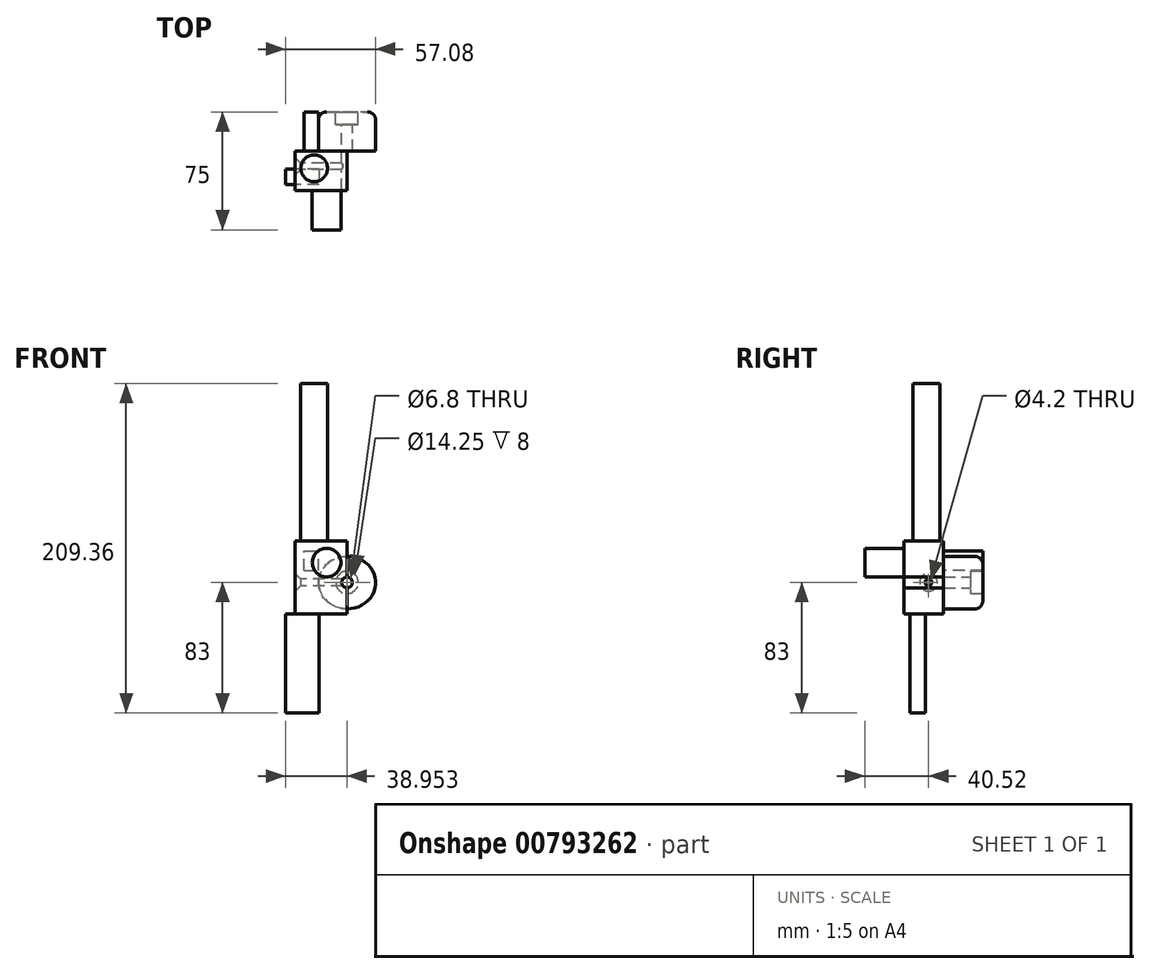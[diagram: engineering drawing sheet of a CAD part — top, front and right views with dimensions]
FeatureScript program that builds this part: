
annotation { "Feature Type Name" : "Feature", "Feature Type Description" : "" }
export const myFeature = defineFeature(function(context is Context, id is Id, definition is map)
    precondition{}
    {
        {
            var Q0;
            Q0=qCreatedBy(makeId("Front.planeOp"),FACE);
            var sketch = newSketch(context, id + "F0", { "sketchPlane" : qUnion([Q0])});
            skLineSegment(sketch, "E0.top", {"start": v(12.98, -20) * mm, "end": v(-20, -20) * mm});
            skLineSegment(sketch, "E0.left", {"start": v(12.98, 26.36) * mm, "end": v(12.98, -20) * mm});
            skLineSegment(sketch, "E0.right", {"start": v(-20, 26.36) * mm, "end": v(-20, -20) * mm});
            skLineSegment(sketch, "E1", {"start": v(12.98, 26.36) * mm, "end": v(-20, 26.36) * mm});
            skSolve(sketch);
        }
        {
            var Q0;
            Q0 = qSketchRegion(id + "F0", true);
            extrude(context, id + "F1", {"entities" : qUnion([Q0]), "depth" : 25 * mm, "offsetDistance" : 25 * mm});
        }
        {
            var Q0;
            Q0=makeQuery(id+"F1.opExtrude","CAP_FACE",FACE,{"disambiguationData":[OSD([sQuery(id+"F0.wireOp",EDGE,"E0.top"),sQuery(id+"F0.wireOp",EDGE,"E0.left"),sQuery(id+"F0.wireOp",EDGE,"E0.right"),sQuery(id+"F0.wireOp",EDGE,"E1")])],"isStart":false});
            var sketch = newSketch(context, id + "F2", { "sketchPlane" : qUnion([Q0])});
            skCircle(sketch, "E2", {"center": v(0, 12.57) * mm, "radius": 9.08 * mm});
            skSolve(sketch);
        }
        {
            var Q0;
            Q0=makeQuery(id+"F2.imprint","IMPRINT",FACE,{"disambiguationData":[TD([[makeQuery(id+"F2.imprint","IMPRINT",EDGE,{"derivedFrom":sQuery(id+"F2.wireOp",EDGE,"E2")}),1.0]])]});
            extrude(context, id + "F3", {"entities" : qUnion([Q0]), "operationType" : NewBodyOperationType.ADD, "depth" : 25 * mm, "offsetDistance" : 25 * mm});
        }
        {
            var Q0;
            Q0=makeQuery(id+"F1.opExtrude","CAP_FACE",FACE,{"disambiguationData":[OSD([sQuery(id+"F0.wireOp",EDGE,"E0.top"),sQuery(id+"F0.wireOp",EDGE,"E0.left"),sQuery(id+"F0.wireOp",EDGE,"E0.right"),sQuery(id+"F0.wireOp",EDGE,"E1")])],"isStart":true});
            var sketch = newSketch(context, id + "F4", { "sketchPlane" : qUnion([Q0])});
            skEllipse(sketch, "E3", {"center": v(-12.98, -0.13) * mm, "majorRadius": 18.12 * mm, "minorRadius": 16.69 * mm, "majorAxis": v(1, 0)});
            skSolve(sketch);
        }
        {
            var Q0;
            {var subQ0=sQuery(id+"F4.wireOp",EDGE,"E3");var subQ1=makeQuery(id+"F1.opExtrude","CAP_EDGE",EDGE,{"disambiguationData":[OSD([sQuery(id+"F0.wireOp",EDGE,"E0.left")])],"isStart":true});var subQ2=makeQuery(id+"F4.imprint","INTERSECT",VERTEX,{"disambiguationData":[OD(0.0)],"derivedFrom":[subQ1,subQ0]});Q0=makeQuery(id+"F4.imprint","IMPRINT",FACE,{"disambiguationData":[TD([[makeQuery(id+"F4.imprint","IMPRINT",EDGE,{"disambiguationData":[TD([[subQ2,1.0]])],"derivedFrom":subQ0}),1.0]])]});}
            var Q1;
            {var subQ0=sQuery(id+"F4.wireOp",EDGE,"E3");var subQ1=makeQuery(id+"F1.opExtrude","CAP_EDGE",EDGE,{"disambiguationData":[OSD([sQuery(id+"F0.wireOp",EDGE,"E0.left")])],"isStart":true});var subQ2=makeQuery(id+"F4.imprint","INTERSECT",VERTEX,{"disambiguationData":[OD(0.0)],"derivedFrom":[subQ1,subQ0]});Q1=makeQuery(id+"F4.imprint","IMPRINT",FACE,{"disambiguationData":[TD([[makeQuery(id+"F4.imprint","IMPRINT",EDGE,{"disambiguationData":[TD([[subQ2,-1.0]])],"derivedFrom":subQ0}),1.0]])]});}
            extrude(context, id + "F5", {"entities" : qUnion([Q0, Q1]), "operationType" : NewBodyOperationType.ADD, "depth" : 25 * mm, "offsetDistance" : 25 * mm});
        }
        {
            var Q0;
            Q0=makeQuery(id+"F5.opExtrude","CAP_FACE",FACE,{"disambiguationData":[OSD([sQuery(id+"F4.wireOp",EDGE,"E3")])],"isStart":false});
            var sketch = newSketch(context, id + "F6", { "sketchPlane" : qUnion([Q0])});
            skCircle(sketch, "E4", {"center": v(-12.98, 0) * mm, "radius": 7.85 * mm});
            skPoint(sketch, "E4.centerSnap0", {"position": v(-12.98, -16.82) * mm});
            skSolve(sketch);
        }
        {
            var Q0;
            Q0=sQuery(id+"F6.wireOp",VERTEX,"E4.center");
            var Q1;
            Q1=makeQuery(id+"F1.opExtrude","SWEPT_BODY",BODY,{"disambiguationData":[OSD([sQuery(id+"F0.wireOp",EDGE,"E0.top"),sQuery(id+"F0.wireOp",EDGE,"E0.left"),sQuery(id+"F0.wireOp",EDGE,"E0.right"),sQuery(id+"F0.wireOp",EDGE,"E1")])]});
            hole(context, id + "F7", {"style" : HoleStyle.C_BORE, "endStyle" : HoleEndStyle.THROUGH, "standardTappedOrClearance" : lookupTablePath({ "standard" : "ISO", "fit" : "Normal", "engagement" : "75%", "pitch" : "1.25 mm", "size" : "M8", "type" : "Tapped" }), "standardBlindInLast" : lookupTablePath({ "fit" : "Standard", "standard" : "ISO", "engagement" : "75%", "pitch" : "1.25 mm", "size" : "M8", "type" : "Tapped" }), "holeDiameter" : 6.8 * mm, "cBoreDiameter" : 14.25 * mm, "cBoreDepth" : 8 * mm, "majorDiameter" : 8 * mm, "showTappedDepth" : true, "isTappedThrough" : true, "tappedDepth" : 12 * mm, "tapClearance" : 3, "locations" : qUnion([Q0]), "scope" : qUnion([Q1])});
        }
        {
            var Q0;
            Q0=makeQuery(id+"F1.opExtrude","SWEPT_FACE",FACE,{"disambiguationData":[OSD([sQuery(id+"F0.wireOp",EDGE,"E0.right")])]});
            var sketch = newSketch(context, id + "F8", { "sketchPlane" : qUnion([Q0])});
            skPoint(sketch, "E5", {"position": v(9.48, 0) * mm});
            skSolve(sketch);
        }
        {
            var Q0;
            Q0=sQuery(id+"F8.wireOp",VERTEX,"E5");
            var Q1;
            Q1=makeQuery(id+"F1.opExtrude","SWEPT_BODY",BODY,{"disambiguationData":[OSD([sQuery(id+"F0.wireOp",EDGE,"E0.top"),sQuery(id+"F0.wireOp",EDGE,"E0.left"),sQuery(id+"F0.wireOp",EDGE,"E0.right"),sQuery(id+"F0.wireOp",EDGE,"E1")])]});
            hole(context, id + "F9", {"style" : HoleStyle.C_SINK, "endStyle" : HoleEndStyle.THROUGH, "standardTappedOrClearance" : lookupTablePath({ "standard" : "ISO", "fit" : "Normal", "engagement" : "75%", "pitch" : "0.8 mm", "size" : "M5", "type" : "Tapped" }), "standardBlindInLast" : lookupTablePath({ "fit" : "Standard", "standard" : "ISO", "engagement" : "75%", "pitch" : "0.8 mm", "size" : "M5", "type" : "Tapped" }), "holeDiameter" : 4.2 * mm, "cSinkDiameter" : 11.2 * mm, "cSinkAngle" : 90 * degree, "majorDiameter" : 5 * mm, "showTappedDepth" : true, "isTappedThrough" : true, "tappedDepth" : 12 * mm, "tapClearance" : 3, "locations" : qUnion([Q0]), "scope" : qUnion([Q1])});
        }
        {
            var Q0;
            Q0=makeQuery(id+"F1.opExtrude","SWEPT_FACE",FACE,{"disambiguationData":[OSD([sQuery(id+"F0.wireOp",EDGE,"E1")])]});
            var sketch = newSketch(context, id + "F10", { "sketchPlane" : qUnion([Q0])});
            skCircle(sketch, "E6", {"center": v(-7.9, -10.8) * mm, "radius": 8.51 * mm});
            skSolve(sketch);
        }
        {
            var Q0;
            Q0=makeQuery(id+"F10.imprint","IMPRINT",FACE,{"disambiguationData":[TD([[makeQuery(id+"F10.imprint","IMPRINT",EDGE,{"derivedFrom":sQuery(id+"F10.wireOp",EDGE,"E6")}),1.0]])]});
            extrude(context, id + "F11", {"entities" : qUnion([Q0]), "operationType" : NewBodyOperationType.ADD, "depth" : 100 * mm, "offsetDistance" : 25 * mm});
        }
        {
            var Q0;
            Q0=makeQuery(id+"F1.opExtrude","CAP_FACE",FACE,{"disambiguationData":[OSD([sQuery(id+"F0.wireOp",EDGE,"E0.top"),sQuery(id+"F0.wireOp",EDGE,"E0.left"),sQuery(id+"F0.wireOp",EDGE,"E0.right"),sQuery(id+"F0.wireOp",EDGE,"E1")])],"isStart":true});
            var sketch = newSketch(context, id + "F12", { "sketchPlane" : qUnion([Q0])});
            skPoint(sketch, "E7.oppositeSnap0", {"position": v(5.14, -0.13) * mm});
            skLineSegment(sketch, "E7.bottom", {"start": v(14.3, 7.5) * mm, "end": v(5.14, 7.5) * mm});
            skLineSegment(sketch, "E7.top", {"start": v(14.3, 20) * mm, "end": v(5.14, 20) * mm});
            skLineSegment(sketch, "E7.left", {"start": v(14.3, 7.5) * mm, "end": v(14.3, 20) * mm});
            skLineSegment(sketch, "E7.right", {"start": v(5.14, 7.5) * mm, "end": v(5.14, 20) * mm});
            skSolve(sketch);
        }
        {
            var Q0;
            Q0=makeQuery(id+"F12.imprint","IMPRINT",FACE,{"disambiguationData":[TD([[makeQuery(id+"F12.imprint","IMPRINT",EDGE,{"derivedFrom":sQuery(id+"F12.wireOp",EDGE,"E7.bottom")}),-1.0]])]});
            extrude(context, id + "F13", {"entities" : qUnion([Q0]), "operationType" : NewBodyOperationType.ADD, "depth" : 25 * mm, "offsetDistance" : 25 * mm});
        }
        {
            var Q0;
            Q0=makeQuery(id+"F1.opExtrude","SWEPT_FACE",FACE,{"disambiguationData":[OSD([sQuery(id+"F0.wireOp",EDGE,"E0.top")])]});
            var sketch = newSketch(context, id + "F14", { "sketchPlane" : qUnion([Q0])});
            skLineSegment(sketch, "E8.bottom", {"start": v(-4.65, 11.38) * mm, "end": v(-25.97, 11.38) * mm});
            skLineSegment(sketch, "E8.top", {"start": v(-4.65, 21.17) * mm, "end": v(-25.97, 21.17) * mm});
            skLineSegment(sketch, "E8.left", {"start": v(-4.65, 11.38) * mm, "end": v(-4.65, 21.17) * mm});
            skLineSegment(sketch, "E8.right", {"start": v(-25.97, 11.38) * mm, "end": v(-25.97, 21.17) * mm});
            skSolve(sketch);
        }
        {
            var Q0;
            Q0 = qSketchRegion(id + "F14", true);
            extrude(context, id + "F15", {"entities" : qUnion([Q0]), "operationType" : NewBodyOperationType.ADD, "depth" : 63 * mm, "offsetDistance" : 25 * mm});
        }
        {
            var Q0;
            Q0=makeQuery(id+"F5.opExtrude","CAP_EDGE",EDGE,{"disambiguationData":[OSD([sQuery(id+"F4.wireOp",EDGE,"E3")])],"isStart":false});
            fillet(context, id + "F16", {"entities" : qUnion([Q0]), "radius" : 5 * mm, "tangentPropagation" : true, "allowEdgeOverflow" : false});
        }
    });
